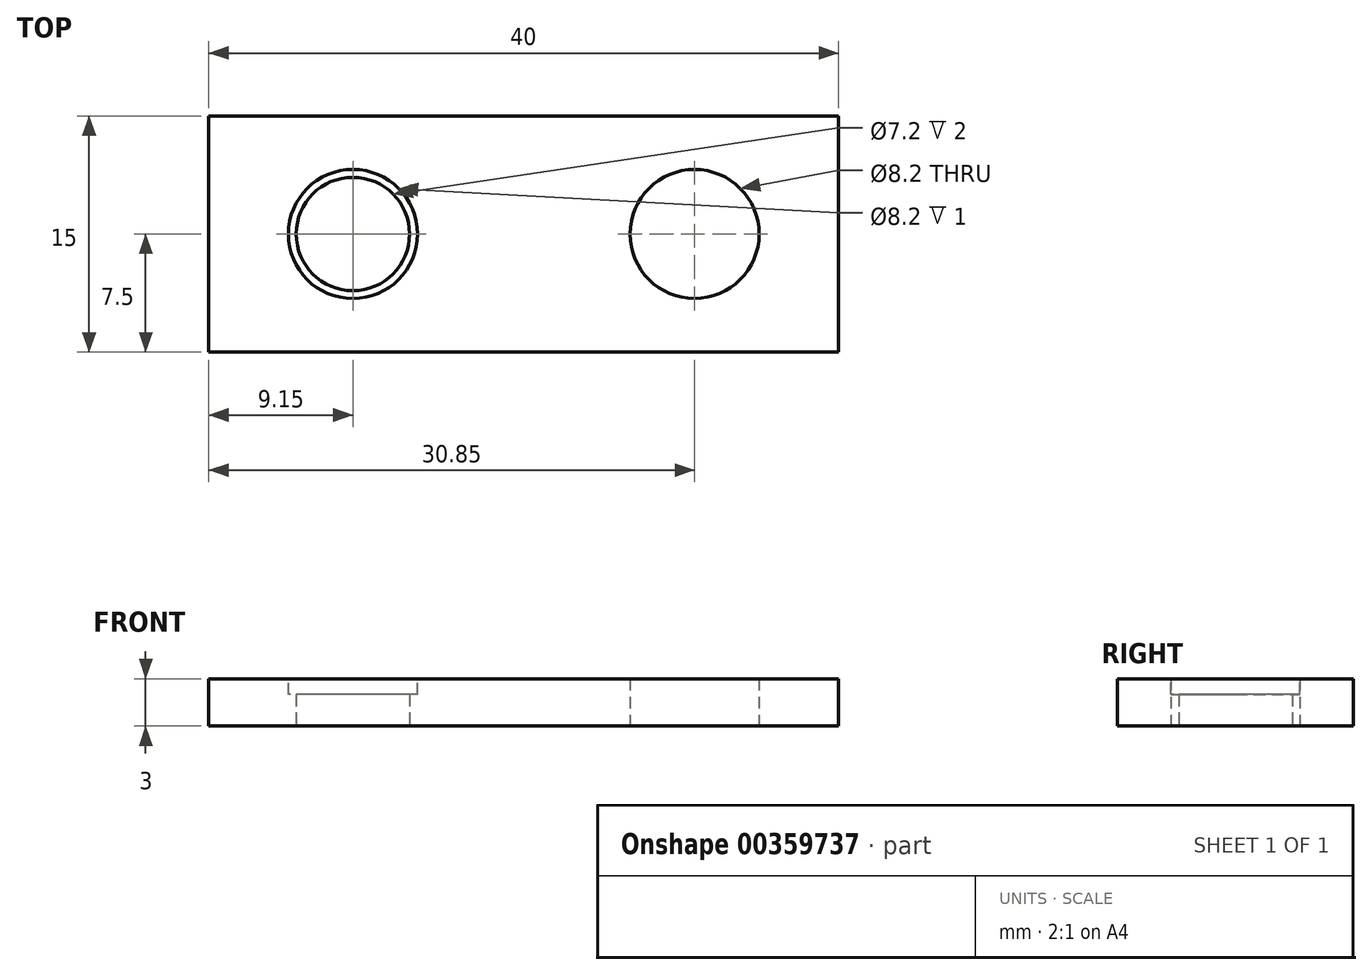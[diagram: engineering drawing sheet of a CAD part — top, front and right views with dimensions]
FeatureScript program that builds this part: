
annotation { "Feature Type Name" : "Feature", "Feature Type Description" : "" }
export const myFeature = defineFeature(function(context is Context, id is Id, definition is map)
    precondition{}
    {
        {
            var Q0;
            Q0=qCreatedBy(makeId("Top.planeOp"),FACE);
            var sketch = newSketch(context, id + "F0", { "sketchPlane" : qUnion([Q0])});
            skLineSegment(sketch, "E0.bottom", {"start": v(20, 7.5) * mm, "end": v(-20, 7.5) * mm});
            skLineSegment(sketch, "E0.top", {"start": v(20, -7.5) * mm, "end": v(-20, -7.5) * mm});
            skLineSegment(sketch, "E0.left", {"start": v(20, 7.5) * mm, "end": v(20, -7.5) * mm});
            skLineSegment(sketch, "E0.right", {"start": v(-20, 7.5) * mm, "end": v(-20, -7.5) * mm});
            skPoint(sketch, "E1.startSnap0", {"position": v(0, 7.5) * mm});
            skPoint(sketch, "E1.endSnap0", {"position": v(0, -7.5) * mm});
            skPoint(sketch, "E2.startSnap0", {"position": v(-20, 0) * mm});
            skLineSegment(sketch, "E3", {"start": v(-10.85, 0) * mm, "end": v(10.85, 0) * mm, "construction": true});
            skPoint(sketch, "E4", {"position": v(0, 0) * mm});
            skLineSegment(sketch, "E5", {"start": v(0, 7.5) * mm, "end": v(0, -7.5) * mm, "construction": true});
            skCircle(sketch, "E6", {"center": v(-10.85, 0) * mm, "radius": 3.6 * mm});
            skCircle(sketch, "E7", {"center": v(-10.85, 0) * mm, "radius": 4.1 * mm});
            skCircle(sketch, "E8.MirrorC", {"center": v(10.85, 0) * mm, "radius": 4.1 * mm});
            skCircle(sketch, "E9.MirrorC", {"center": v(10.85, 0) * mm, "radius": 3.6 * mm});
            skSolve(sketch);
        }
        {
            var Q0;
            Q0 = qSketchRegion(id + "F0", true);
            var Q1;
            Q1=makeQuery(id+"F0.imprint","IMPRINT",FACE,{"disambiguationData":[TD([[makeQuery(id+"F0.imprint","IMPRINT",EDGE,{"derivedFrom":sQuery(id+"F0.wireOp",EDGE,"E8.MirrorC")}),-1.0]])]});
            var Q2;
            Q2=makeQuery(id+"F0.imprint","IMPRINT",FACE,{"disambiguationData":[TD([[makeQuery(id+"F0.imprint","IMPRINT",EDGE,{"derivedFrom":sQuery(id+"F0.wireOp",EDGE,"E6")}),-1.0]])]});
            extrude(context, id + "F1", {"entities" : qUnion([Q0, Q1, Q2]), "depth" : 3 * mm, "offsetDistance" : 25 * mm});
        }
        {
            var Q0;
            Q0=makeQuery(id+"F1.opExtrude","CAP_FACE",FACE,{"disambiguationData":[OSD([sQuery(id+"F0.wireOp",EDGE,"E0.bottom"),sQuery(id+"F0.wireOp",EDGE,"E0.top"),sQuery(id+"F0.wireOp",EDGE,"E0.left"),sQuery(id+"F0.wireOp",EDGE,"E0.right"),sQuery(id+"F0.wireOp",EDGE,"E6"),sQuery(id+"F0.wireOp",EDGE,"E9.MirrorC")])],"isStart":false});
            var sketch = newSketch(context, id + "F2", { "sketchPlane" : qUnion([Q0])});
            skCircle(sketch, "E10.0", {"center": v(-10.85, 0) * mm, "radius": 4.1 * mm});
            skCircle(sketch, "E10.1", {"center": v(10.85, 0) * mm, "radius": 4.1 * mm});
            skSolve(sketch);
        }
        {
            var Q0;
            Q0 = qSketchRegion(id + "F2", true);
            extrude(context, id + "F3", {"entities" : qUnion([Q0]), "operationType" : NewBodyOperationType.REMOVE, "oppositeDirection" : true, "depth" : 1 * mm, "offsetDistance" : 25 * mm});
        }
    });
